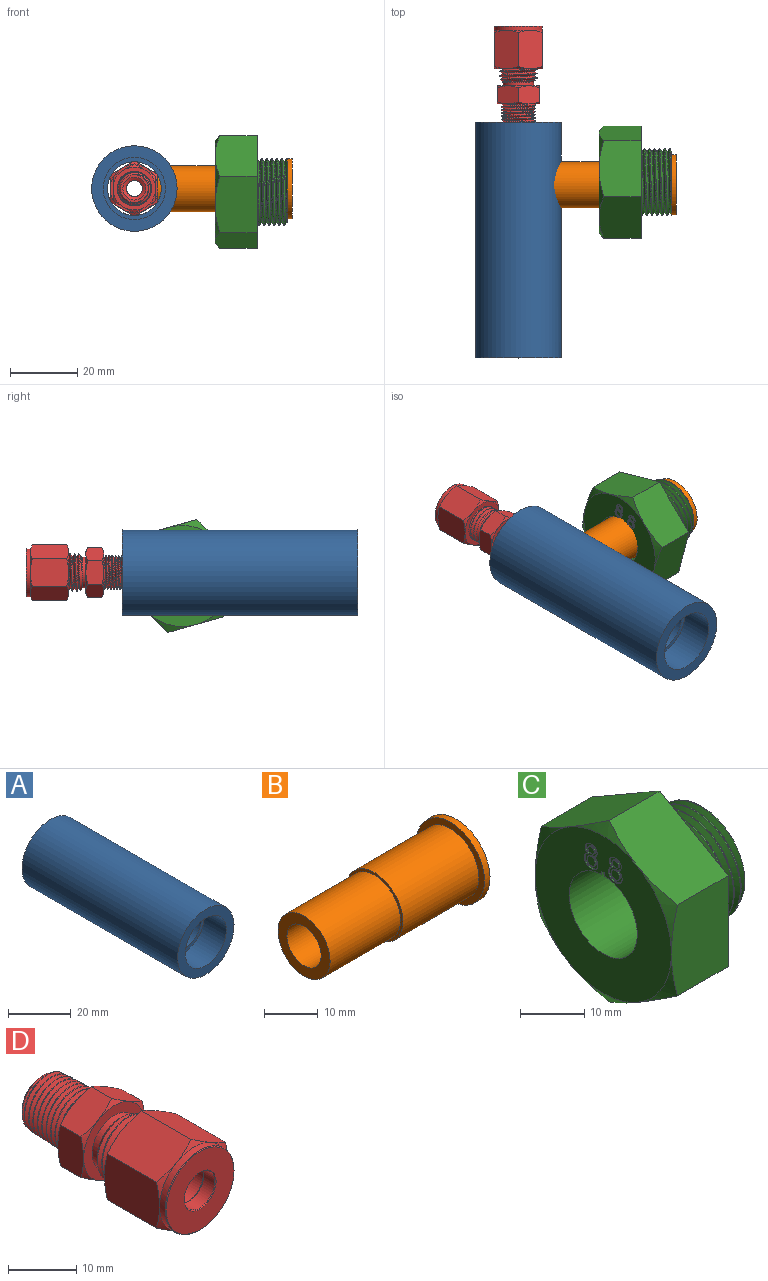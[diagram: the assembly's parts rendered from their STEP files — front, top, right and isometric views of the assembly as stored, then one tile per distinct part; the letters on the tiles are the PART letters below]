
ASSEMBLY  parts=4 mates=3
PART A: 9 faces, bbox 25.4x70x25.4 mm
  f0: cylinder r=8mm len=16mm, axis (0,1,0), area 150.8mm2, adj f5,f7
  f1: cylinder r=12.7mm len=70mm, axis (0,1,0), area 5486.5mm2, adj f2,f3,f6
  f2: plane 25.4x25.4mm, normal (0,-1,0), area 237.9mm2, adj f1,f4
  f3: plane 25.4x25.4mm, normal (0,1,0), area 256.2mm2, adj f1,f8
  f4: cylinder r=9.25mm len=18.5mm, axis (0,-1,0), area 581.2mm2, adj f2,f5
  f5: plane 18.5x18.5mm, normal (0,-1,0), area 67.7mm2, adj f0,f4
  f6: cylinder r=5.56mm len=11.11mm, axis (-1,0,0), area 142.5mm2, adj f1,f8
  f7: plane 17.86x17.86mm, normal (0,1,0), area 49.5mm2, adj f0,f8
  f8: cylinder r=8.93mm len=57mm, axis (0,1,0), area 3095.6mm2, adj f3,f6,f7
PART B: 8 faces, bbox 40x17.9x17.9 mm
  f0: plane 17.88x17.88mm, normal (-1,0,0), area 75.5mm2, adj f1,f6
  f1: cylinder r=7.47mm len=20mm, axis (1,0,0), area 939.3mm2, adj f0,f2
  f2: plane 14.95x14.95mm, normal (-1,0,0), area 27.8mm2, adj f1,f3
  f3: cylinder r=6.86mm len=18.54mm, axis (1,0,0), area 798.9mm2, adj f2,f4
  f4: plane 13.72x13.72mm, normal (-1,0,0), area 84.1mm2, adj f3,f7
  f5: plane 17.88x17.88mm, normal (1,0,0), area 187.5mm2, adj f6,f7
  f6: cylinder r=8.94mm len=17.88mm, axis (1,0,0), area 82mm2, adj f0,f5
  f7: cylinder r=4.5mm len=40mm, axis (-1,0,0), area 1131mm2, adj f4,f5
PART C: 62 faces, bbox 23.7x36.1x36.1 mm
  f0: plane 30x30mm, normal (-1,0,0), area 508.1mm2, adj f12,f13,f14,f15,f16,f17,f18,f19
  f1: plane 18.76x13.94mm, normal (0,1,0), area 208.5mm2, adj f2,f6,f11,f14,f15
  f2: plane 16.42x13.93mm, normal (0,0.5,-0.87), area 208.5mm2, adj f1,f3,f11,f13,f14
  f3: plane 16.42x13.93mm, normal (0,-0.5,-0.87), area 208.5mm2, adj f2,f4,f11,f12,f13
  f4: plane 18.76x13.94mm, normal (0,-1,0), area 208.5mm2, adj f3,f5,f11,f12,f17
  f5: plane 16.42x13.93mm, normal (0,-0.5,0.87), area 208.5mm2, adj f4,f6,f11,f16,f17
  f6: plane 16.42x13.93mm, normal (0,0.5,0.87), area 208.5mm2, adj f1,f5,f11,f15,f16
  f7: cylinder r=10mm len=20mm, axis (1,0,0), area 71mm2, adj f9,f10,f11,f60
  f8: cylinder r=9.03mm len=18.05mm, axis (1,0,0), area 64.1mm2, adj f9,f10,f11,f60
  f9: bspline ~20x20mm, area 404.3mm2, adj f7,f8,f11,f60
  f10: bspline ~20x20mm, area 404.3mm2, adj f7,f8,f11,f60
  f11: plane 35.25x30.6mm, normal (1,0,0), area 494.7mm2, adj f1,f2,f3,f4,f5,f6,f7,f8
  f12: cone r=15mm half-angle=60deg, axis (1,0,0), area 22.1mm2, adj f0,f3,f4
  f13: cone r=15mm half-angle=60deg, axis (1,0,0), area 22.1mm2, adj f0,f2,f3
  f14: cone r=15mm half-angle=60deg, axis (1,0,0), area 22.1mm2, adj f0,f1,f2
  f15: cone r=15mm half-angle=60deg, axis (1,0,0), area 22.1mm2, adj f0,f1,f6
  f16: cone r=15mm half-angle=60deg, axis (1,0,0), area 22.1mm2, adj f0,f5,f6
  f17: cone r=15mm half-angle=60deg, axis (1,0,0), area 22.1mm2, adj f0,f4,f5
  f18: extruded ~1.17x0.88mm, area 0.4mm2, adj f0,f19,f25,f26
  f19: extruded ~0.92x0.7mm, area 0.3mm2, adj f0,f18,f20,f26
  f20: extruded ~1.3x1.17mm, area 0.5mm2, adj f0,f19,f21,f26
  f21: extruded ~1.31x1.18mm, area 0.5mm2, adj f0,f20,f22,f26
  f22: extruded ~0.91x0.69mm, area 0.3mm2, adj f0,f21,f23,f26
  f23: extruded ~1.19x0.86mm, area 0.4mm2, adj f0,f22,f24,f26
  f24: extruded ~1.48x1.41mm, area 0.6mm2, adj f0,f23,f25,f26
  f25: extruded ~1.48x1.42mm, area 0.6mm2, adj f0,f18,f24,f26
  f26: plane 4.68x2.96mm, normal (-1,0,0), area 6.8mm2, adj f18,f19,f20,f21,f22,f23,f24,f25
  f27: extruded ~0.71x0.64mm, area 0.3mm2, adj f26,f28,f30,f35
  f28: extruded ~0.71x0.66mm, area 0.3mm2, adj f26,f27,f29,f35
  f29: extruded ~0.71x0.64mm, area 0.3mm2, adj f26,f28,f30,f35
  f30: extruded ~0.72x0.67mm, area 0.3mm2, adj f26,f27,f29,f35
  f31: extruded ~0.88x0.88mm, area 0.3mm2, adj f26,f32,f34,f36
  f32: extruded ~0.9x0.9mm, area 0.4mm2, adj f26,f31,f33,f36
  f33: extruded ~0.88x0.88mm, area 0.4mm2, adj f26,f32,f34,f36
  f34: extruded ~0.9x0.89mm, area 0.4mm2, adj f26,f31,f33,f36
  f35: plane 1.42x1.3mm, normal (-1,0,0), area 1.5mm2, adj f27,f28,f29,f30
  f36: plane 1.78x1.78mm, normal (-1,0,0), area 2.6mm2, adj f31,f32,f33,f34
  f37: plane 0.61x0.26mm, normal (0,-1,0), area 0.1mm2, adj f0,f38,f40,f61
  f38: plane 0.59x0.25mm, normal (0,0,-1), area 0.1mm2, adj f0,f37,f39,f40
  f39: plane 0.61x0.26mm, normal (0,1,0), area 0.1mm2, adj f0,f38,f40,f61
  f40: plane 0.61x0.6mm, normal (-1,0,0), area 0.4mm2, adj f37,f38,f39,f61
  f41: extruded ~1.17x0.88mm, area 0.4mm2, adj f0,f42,f48,f49
  f42: extruded ~0.92x0.7mm, area 0.3mm2, adj f0,f41,f43,f49
  f43: extruded ~1.3x1.17mm, area 0.5mm2, adj f0,f42,f44,f49
  f44: extruded ~1.31x1.18mm, area 0.5mm2, adj f0,f43,f45,f49
  f45: extruded ~0.91x0.69mm, area 0.3mm2, adj f0,f44,f46,f49
  f46: extruded ~1.19x0.86mm, area 0.4mm2, adj f0,f45,f47,f49
  f47: extruded ~1.48x1.41mm, area 0.6mm2, adj f0,f46,f48,f49
  f48: extruded ~1.48x1.42mm, area 0.6mm2, adj f0,f41,f47,f49
  f49: plane 4.68x2.96mm, normal (-1,0,0), area 6.8mm2, adj f41,f42,f43,f44,f45,f46,f47,f48
  f50: extruded ~0.71x0.64mm, area 0.3mm2, adj f49,f51,f53,f58
  f51: extruded ~0.71x0.66mm, area 0.3mm2, adj f49,f50,f52,f58
  f52: extruded ~0.71x0.64mm, area 0.3mm2, adj f49,f51,f53,f58
  f53: extruded ~0.72x0.67mm, area 0.3mm2, adj f49,f50,f52,f58
  f54: extruded ~0.88x0.88mm, area 0.3mm2, adj f49,f55,f57,f59
  f55: extruded ~0.9x0.9mm, area 0.4mm2, adj f49,f54,f56,f59
  f56: extruded ~0.88x0.88mm, area 0.4mm2, adj f49,f55,f57,f59
  f57: extruded ~0.9x0.89mm, area 0.4mm2, adj f49,f54,f56,f59
  f58: plane 1.42x1.3mm, normal (-1,0,0), area 1.5mm2, adj f50,f51,f52,f53
  f59: plane 1.78x1.78mm, normal (-1,0,0), area 2.6mm2, adj f54,f55,f56,f57
  f60: plane 19.65x19.64mm, normal (1,0,0), area 108mm2, adj f7,f8,f9,f10,f61
  f61: cylinder r=7.5mm len=21.5mm, axis (1,0,0), area 1013mm2, adj f0,f37,f39,f40,f60
PART D: 81 faces, bbox 17.2x33.7x17.2 mm
  f0: plane 14.29x14.29mm, normal (0,1,0), area 63.3mm2, adj f2,f3,f4,f5,f6,f7,f22,f23
  f1: plane 14.03x14.03mm, normal (0,-1,0), area 120.4mm2, adj f30,f31
  f2: cone r=8.25mm half-angle=60deg, axis (0,-1,0), area 5mm2, adj f0,f9,f10
  f3: cone r=8.25mm half-angle=60deg, axis (0,-1,0), area 5mm2, adj f0,f10,f11
  f4: cone r=8.25mm half-angle=60deg, axis (0,-1,0), area 5mm2, adj f0,f11,f12
  f5: cone r=8.25mm half-angle=60deg, axis (0,-1,0), area 5mm2, adj f0,f12,f13
  f6: cone r=8.25mm half-angle=60deg, axis (0,-1,0), area 5mm2, adj f0,f8,f13
  f7: cone r=8.25mm half-angle=60deg, axis (0,-1,0), area 5mm2, adj f0,f8,f9
  f8: plane 12.12x7.82mm, normal (0.5,0,0.87), area 90.7mm2, adj f6,f7,f9,f13,f15,f20
  f9: plane 12.11x8.93mm, normal (1,0,0), area 90.7mm2, adj f2,f7,f8,f10,f19,f20
  f10: plane 12.12x7.82mm, normal (0.5,0,-0.87), area 90.7mm2, adj f2,f3,f9,f11,f18,f19
  f11: plane 12.12x7.82mm, normal (-0.5,0,-0.87), area 90.7mm2, adj f3,f4,f10,f12,f17,f18
  f12: plane 12.11x8.93mm, normal (-1,0,0), area 90.7mm2, adj f4,f5,f11,f13,f16,f17
  f13: plane 12.12x7.82mm, normal (-0.5,0,0.87), area 90.7mm2, adj f5,f6,f8,f12,f15,f16
  f14: cylinder r=7.14mm len=14.29mm, axis (0,-1,0), area 51.3mm2, adj f15,f16,f17,f18,f19,f20,f31
  f15: cone r=7.14mm half-angle=60deg, axis (0,1,0), area 5mm2, adj f8,f13,f14
  f16: cone r=7.14mm half-angle=60deg, axis (0,1,0), area 5mm2, adj f12,f13,f14
  f17: cone r=7.14mm half-angle=60deg, axis (0,1,0), area 5mm2, adj f11,f12,f14
  f18: cone r=7.14mm half-angle=60deg, axis (0,1,0), area 5mm2, adj f10,f11,f14
  f19: cone r=7.14mm half-angle=60deg, axis (0,1,0), area 5mm2, adj f9,f10,f14
  f20: cone r=7.14mm half-angle=60deg, axis (0,1,0), area 5mm2, adj f8,f9,f14
  f21: cylinder r=3.17mm len=6.35mm, axis (0,-1,0), area 45.6mm2, adj f29,f30
  f22: cylinder r=5.56mm len=11.11mm, axis (0,-1,0), area 15.1mm2, adj f0,f23,f47
  f23: cylinder r=5.56mm len=11.11mm, axis (0,-1,0), area 38.7mm2, adj f0,f22,f24,f47,f49
  f24: cylinder r=5.56mm len=11.11mm, axis (0,-1,0), area 38.8mm2, adj f23,f25,f47,f49
  f25: cylinder r=5.56mm len=11.11mm, axis (0,-1,0), area 154.3mm2, adj f24,f26,f46,f47,f49
  f26: plane 11.11x11.11mm, normal (0,1,0), area 20.9mm2, adj f25,f27
  f27: cylinder r=4.92mm len=9.84mm, axis (0,-1,0), area 78.5mm2, adj f26,f28
  f28: plane 9.84x9.84mm, normal (0,1,0), area 7.8mm2, adj f27,f74
  f29: cone r=3.3mm half-angle=45deg, axis (0,1,0), area 3.7mm2, adj f21,f33
  f30: cone r=3.17mm half-angle=45deg, axis (0,-1,0), area 3.7mm2, adj f1,f21
  f31: cone r=7.02mm half-angle=45deg, axis (0,1,0), area 8mm2, adj f1,f14
  f32: cylinder r=5.56mm len=11.11mm, axis (0,1,0), area 13.2mm2, adj f0,f44,f47,f49
  f33: plane 6.6x6.6mm, normal (0,-1,0), area 2.6mm2, adj f29,f77
  f34: cone r=3.17mm half-angle=12.6deg, axis (0,-1,0), area 42.1mm2, adj f69,f80
  f35: cylinder r=2.37mm len=6.93mm, axis (0,-1,0), area 103.5mm2, adj f68,f73
  f36: plane 8.24x8.24mm, normal (0,1,0), area 16.7mm2, adj f70,f72
  f37: cone r=4.83mm half-angle=1.8deg, axis (0,-1,0), area 35.9mm2, adj f39,f40,f42,f70,f71
  f38: bspline ~9.85x9.11mm, area 32.8mm2, adj f39,f40,f42,f70
  f39: bspline ~10.43x10.41mm, area 133.9mm2, adj f37,f38,f42,f70
  f40: bspline ~10.45x10.44mm, area 203.9mm2, adj f37,f38,f42,f70,f71
  f41: plane 9.19x9.19mm, normal (0,-1,0), area 14.9mm2, adj f46,f78
  f42: plane 13.05x13.05mm, normal (0,1,0), area 53mm2, adj f37,f38,f39,f40,f62,f63,f64,f65
  f43: plane 12.7x12.7mm, normal (0,-1,0), area 60.4mm2, adj f45,f50,f51,f52,f53,f54,f55
  f44: cone r=5.69mm half-angle=45deg, axis (0,-1,0), area 24.2mm2, adj f32,f45,f47,f48,f49
  f45: cylinder r=4.59mm len=9.19mm, axis (0,-1,0), area 31.7mm2, adj f43,f44
  f46: cone r=4.59mm half-angle=45deg, axis (0,1,0), area 24.2mm2, adj f25,f41,f47,f48,f49
  f47: bspline ~11.11x11.11mm, area 198.4mm2, adj f22,f23,f24,f25,f32,f44,f46,f48
  f48: cylinder r=4.73mm len=9.46mm, axis (0,-1,0), area -0.6mm2, adj f44,f46,f47,f49
  f49: bspline ~11.25x11.25mm, area 197.9mm2, adj f23,f24,f25,f32,f44,f46,f48
  f50: cone r=6.35mm half-angle=60deg, axis (0,1,0), area 4mm2, adj f43,f59,f60
  f51: cone r=6.35mm half-angle=60deg, axis (0,1,0), area 4mm2, adj f43,f58,f59
  f52: cone r=6.35mm half-angle=60deg, axis (0,1,0), area 4mm2, adj f43,f57,f58
  f53: cone r=6.35mm half-angle=60deg, axis (0,1,0), area 4mm2, adj f43,f56,f57
  f54: cone r=6.35mm half-angle=60deg, axis (0,1,0), area 4mm2, adj f43,f56,f61
  f55: cone r=6.35mm half-angle=60deg, axis (0,1,0), area 4mm2, adj f43,f60,f61
  f56: plane 6.95x5.95mm, normal (0.5,0,0.87), area 36.3mm2, adj f53,f54,f57,f61,f65,f66
  f57: plane 7.94x5.94mm, normal (1,0,0), area 36.3mm2, adj f52,f53,f56,f58,f64,f65
  f58: plane 6.95x5.95mm, normal (0.5,0,-0.87), area 36.3mm2, adj f51,f52,f57,f59,f63,f64
  f59: plane 6.95x5.95mm, normal (-0.5,0,-0.87), area 36.3mm2, adj f50,f51,f58,f60,f62,f63
  f60: plane 7.94x5.94mm, normal (-1,0,0), area 36.3mm2, adj f50,f55,f59,f61,f62,f67
  f61: plane 6.95x5.95mm, normal (-0.5,0,0.87), area 36.3mm2, adj f54,f55,f56,f60,f66,f67
  f62: cone r=7.33mm half-angle=60deg, axis (0,-1,0), area 4mm2, adj f42,f59,f60
  f63: cone r=7.33mm half-angle=60deg, axis (0,-1,0), area 4mm2, adj f42,f58,f59
  f64: cone r=7.33mm half-angle=60deg, axis (0,-1,0), area 4mm2, adj f42,f57,f58
  f65: cone r=7.33mm half-angle=60deg, axis (0,-1,0), area 4mm2, adj f42,f56,f57
  f66: cone r=7.33mm half-angle=60deg, axis (0,-1,0), area 4mm2, adj f42,f56,f61
  f67: cone r=7.33mm half-angle=60deg, axis (0,-1,0), area 4mm2, adj f42,f60,f61
  f68: plane 6.35x6.35mm, normal (0,-1,0), area 14mm2, adj f35,f69
  f69: cylinder r=3.17mm len=6.35mm, axis (0,-1,0), area 79.6mm2, adj f34,f68
  f70: cone r=4.94mm half-angle=45deg, axis (0,-1,0), area 16.8mm2, adj f36,f37,f38,f39,f40,f71
  f71: cone r=4.94mm half-angle=45deg, axis (0,-1,0), area 0mm2, adj f37,f40,f70
  f72: cylinder r=3.42mm len=9.97mm, axis (0,-1,0), area 213.9mm2, adj f36,f73
  f73: cone r=3.42mm half-angle=59deg, axis (0,1,0), area 22.1mm2, adj f35,f72
  f74: cylinder r=4.66mm len=9.32mm, axis (0,-1,0), area 29.8mm2, adj f28,f75
  f75: plane 9.32x9.32mm, normal (0,1,0), area 21.4mm2, adj f74,f76
  f76: cylinder r=3.86mm len=7.72mm, axis (0,-1,0), area 21.6mm2, adj f75,f79
  f77: cylinder r=3.17mm len=6.78mm, axis (0,-1,0), area 135.3mm2, adj f33,f80
  f78: cone r=3.61mm half-angle=12.6deg, axis (0,-1,0), area 82.2mm2, adj f41,f79
  f79: plane 9.4x9.4mm, normal (0,-1,0), area 22.5mm2, adj f76,f78
  f80: plane 7.21x7.21mm, normal (0,1,0), area 9.2mm2, adj f34,f77
PLACE A t=(-2.73,-1.14,0.66)mm fixed
PLACE B t=(24.23,15.31,0.66)mm
PLACE C rot(axis=(1,0,0),14.3deg) t=(42.52,16.08,-0.37)mm
PLACE D rot(axis=(1,0,0),180deg) t=(-2.73,62.52,0.66)mm
MATE fastened D.f2 <-> A.f1  axis (0,-1,0) through (-2.73,29.75,0.66)mm
MATE revolute C.f60 <-> B.f1  axis (1,0,0) through (42.77,15.31,0.66)mm
MATE fastened B.f1 <-> A.f6  axis (-1,0,0) through (4.23,15.31,0.66)mm
